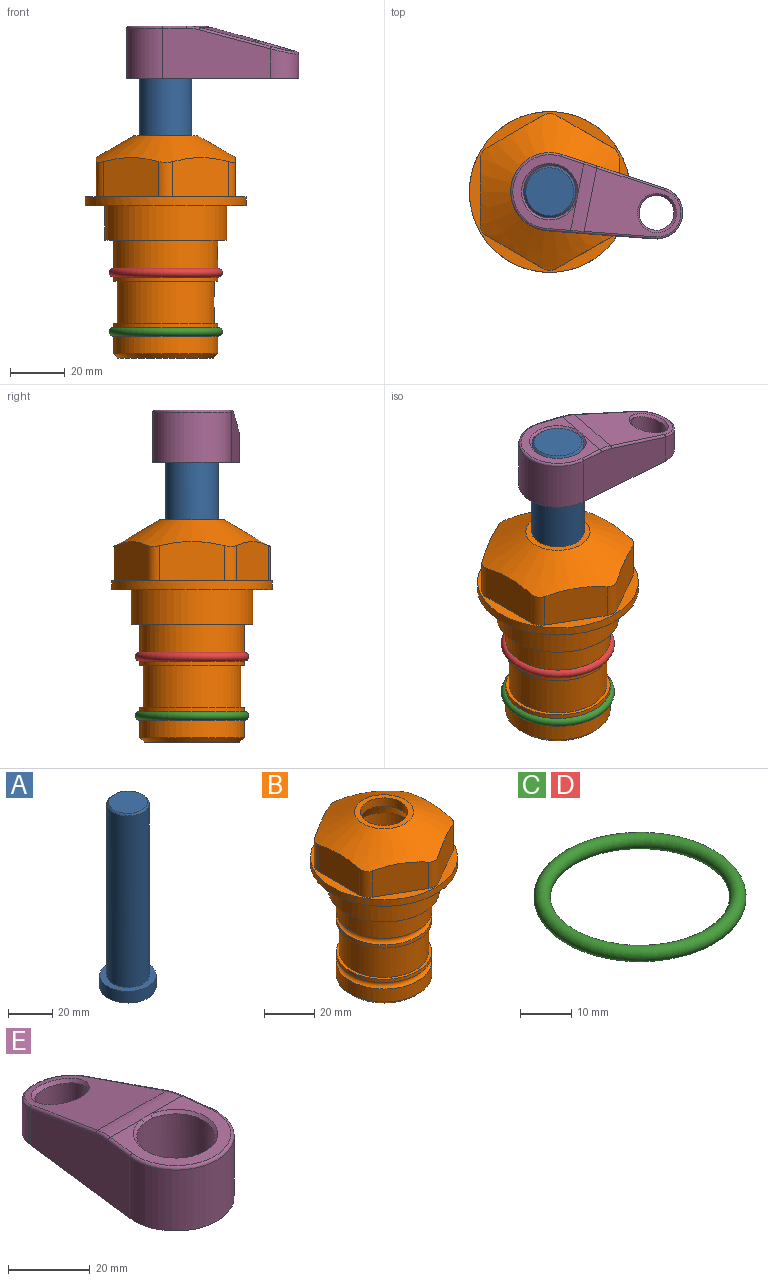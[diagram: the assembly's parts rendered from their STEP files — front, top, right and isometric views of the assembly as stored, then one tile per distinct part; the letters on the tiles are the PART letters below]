
ASSEMBLY  parts=5 mates=4
PART A: 6 faces, bbox 25.4x25.4x101.6 mm
  f0: plane 17.46x17.46mm, normal (0,0,1), area 239.5mm2, adj f5
  f1: plane 25.4x25.4mm, normal (0,0,-1), area 506.7mm2, adj f2
  f2: cylinder r=12.7mm len=25.4mm, axis (0,0,1), area 506.7mm2, adj f1,f3
  f3: plane 25.4x25.4mm, normal (0,0,1), area 221.7mm2, adj f2,f4
  f4: cylinder r=9.53mm len=94.46mm, axis (0,0,1), area 5653mm2, adj f3,f5
  f5: cone r=8.73mm half-angle=45deg, axis (0,0,-1), area 64.4mm2, adj f0,f4
PART B: 36 faces, bbox 58.7x58.7x81 mm
  f0: cylinder r=17.78mm len=35.56mm, axis (0,0,1), area 1670.8mm2, adj f23,f24,f31
  f1: cylinder r=19.05mm len=38.1mm, axis (0,0,1), area 1191.9mm2, adj f26,f27,f30
  f2: plane 58.66x58.66mm, normal (0,0,-1), area 1150.6mm2, adj f3,f28
  f3: cylinder r=29.33mm len=58.66mm, axis (0,0,-1), area 585.1mm2, adj f2,f4
  f4: plane 58.66x58.66mm, normal (0,0,1), area 475.9mm2, adj f3,f5,f6,f7,f8,f9,f10,f11
  f5: plane 20.32x14.34mm, normal (-0.5,0.87,0), area 324.4mm2, adj f4,f15,f16,f17
  f6: plane 20.32x14.34mm, normal (0.5,0.87,0), area 324.4mm2, adj f4,f14,f15,f17
  f7: plane 23.48x14.34mm, normal (1,0,0), area 324.4mm2, adj f4,f13,f14,f17
  f8: plane 20.32x14.34mm, normal (0.5,-0.87,0), area 324.4mm2, adj f4,f12,f13,f17
  f9: plane 20.32x14.34mm, normal (-0.5,-0.87,0), area 324.4mm2, adj f4,f11,f12,f17
  f10: plane 23.48x14.34mm, normal (-1,0,0), area 324.4mm2, adj f4,f11,f16,f17
  f11: cylinder r=5.08mm len=12.85mm, axis (0,0,-1), area 67.2mm2, adj f4,f9,f10,f17
  f12: cylinder r=5.08mm len=12.85mm, axis (0,0,-1), area 67.2mm2, adj f4,f8,f9,f17
  f13: cylinder r=5.08mm len=12.85mm, axis (0,0,-1), area 67.2mm2, adj f4,f7,f8,f17
  f14: cylinder r=5.08mm len=12.85mm, axis (0,0,-1), area 67.2mm2, adj f4,f6,f7,f17
  f15: cylinder r=5.08mm len=12.85mm, axis (0,0,-1), area 67.2mm2, adj f4,f5,f6,f17
  f16: cylinder r=5.08mm len=12.85mm, axis (0,0,-1), area 67.2mm2, adj f4,f5,f10,f17
  f17: cone r=11.73mm half-angle=60deg, axis (0,0,-1), area 2071.8mm2, adj f5,f6,f7,f8,f9,f10,f11,f12
  f18: plane 23.46x23.46mm, normal (0,0,1), area 147.4mm2, adj f17,f35
  f19: plane 34.93x34.93mm, normal (0,0,-1), area 958mm2, adj f29
  f20: cylinder r=19.05mm len=38.1mm, axis (0,0,1), area 760.1mm2, adj f21,f29
  f21: torus R=19.05mm, axis (0,0,1), area 565.3mm2, adj f20,f22
  f22: cylinder r=19.05mm len=38.1mm, axis (0,0,1), area 190mm2, adj f21,f23
  f23: plane 38.1x38.1mm, normal (0,0,1), area 146.9mm2, adj f0,f22
  f24: plane 38.1x38.1mm, normal (0,0,-1), area 146.9mm2, adj f0,f25
  f25: cylinder r=19.05mm len=38.1mm, axis (0,0,1), area 190mm2, adj f24,f26
  f26: torus R=19.05mm, axis (0,0,1), area 565.3mm2, adj f1,f25
  f27: plane 44.45x44.45mm, normal (0,0,-1), area 411.7mm2, adj f1,f28
  f28: cylinder r=22.23mm len=44.45mm, axis (0,0,1), area 1773.5mm2, adj f2,f27
  f29: cone r=19.05mm half-angle=45deg, axis (0,0,1), area 257.5mm2, adj f19,f20
  f30: cylinder r=3.17mm len=6.75mm, axis (-1,0,0), area 128mm2, adj f1,f33
  f31: cylinder r=3.17mm len=6.35mm, axis (-1,0,0), area 102.5mm2, adj f0,f33
  f32: plane 25.4x25.4mm, normal (0,0,1), area 506.7mm2, adj f33
  f33: cylinder r=12.7mm len=66.42mm, axis (0,0,-1), area 5236.2mm2, adj f30,f31,f32,f34
  f34: cone r=9.53mm half-angle=30deg, axis (0,0,-1), area 443.4mm2, adj f33,f35
  f35: cylinder r=9.53mm len=19.05mm, axis (0,0,-1), area 240.9mm2, adj f18,f34
PART C: 1 faces, bbox 44.7x44.7x3.2 mm
  f0: torus R=19.05mm, axis (0,0,1), area 1193.9mm2
PART D: same geometry as C
PART E: 31 faces, bbox 31.7x65.5x19.8 mm
  f0: plane 39.12x18.26mm, normal (0.99,0.12,0), area 612.2mm2, adj f1,f4,f7,f11,f13,f15
  f1: cylinder r=9.53mm len=18.91mm, axis (0,0,-1), area 296.1mm2, adj f0,f2,f7,f17
  f2: plane 39.12x18.26mm, normal (-0.99,0.12,0), area 612.2mm2, adj f1,f4,f7,f12,f14,f16
  f3: cylinder r=6.35mm len=12.7mm, axis (0,0,-1), area 362.4mm2, adj f7,f18
  f4: cylinder r=14.29mm len=28.58mm, axis (0,0,-1), area 882.2mm2, adj f0,f2,f7,f10
  f5: cylinder r=9.53mm len=19.05mm, axis (0,0,-1), area 1092.6mm2, adj f7,f19,f20
  f6: plane 26.99x23.69mm, normal (0,0,1), area 216.2mm2, adj f9,f10,f11,f12,f19
  f7: plane 63.5x28.58mm, normal (0,0,-1), area 661.8mm2, adj f0,f1,f2,f3,f4,f5,f22,f23
  f8: plane 33.52x23.6mm, normal (0,0.26,0.97), area 486mm2, adj f9,f15,f16,f17,f18
  f9: cylinder r=19.05mm len=24.72mm, axis (1,0,0), area 120.4mm2, adj f6,f8,f13,f14,f20
  f10: torus R=13.49mm, axis (0,0,1), area 59mm2, adj f4,f6,f11,f12
  f11: cylinder r=0.79mm len=8.67mm, axis (0.12,-0.99,0), area 10.8mm2, adj f0,f6,f10,f13
  f12: cylinder r=0.79mm len=8.67mm, axis (0.12,0.99,0), area 10.8mm2, adj f2,f6,f10,f14
  f13: bspline ~4.95x1.42mm, area 6.1mm2, adj f0,f9,f11,f15
  f14: bspline ~4.95x1.42mm, area 6.1mm2, adj f2,f9,f12,f16
  f15: cylinder r=0.79mm len=25.95mm, axis (0.12,-0.96,0.26), area 32.9mm2, adj f0,f8,f13,f17
  f16: cylinder r=0.79mm len=25.95mm, axis (0.12,0.96,-0.26), area 32.9mm2, adj f2,f8,f14,f17
  f17: bspline ~18.91x8.38mm, area 30mm2, adj f1,f8,f15,f16
  f18: bspline ~14.29x14.29mm, area 48.3mm2, adj f3,f8
  f19: cone r=9.53mm half-angle=45deg, axis (0,0,1), area 66.5mm2, adj f5,f6,f20
  f20: bspline ~3.22x0.96mm, area 3.5mm2, adj f5,f9,f19
  f21: plane 2.75x2.72mm, normal (0,0,-1), area 2.9mm2, adj f23,f25,f28
  f22: plane 23.05x15.88mm, normal (-0.99,-0.12,0), area 323.6mm2, adj f7,f25,f26,f27,f28,f29
  f23: plane 23.05x15.88mm, normal (0.99,-0.12,0), area 323.6mm2, adj f7,f21,f25,f27,f28,f30
  f24: cylinder r=9.53mm len=10.69mm, axis (0,0,-1), area 114.7mm2, adj f7,f27,f29,f30
  f25: cylinder r=12.7mm len=20.59mm, axis (0,0,-1), area 381.1mm2, adj f7,f21,f22,f23,f26,f28
  f26: plane 2.75x2.72mm, normal (0,0,-1), area 2.9mm2, adj f22,f25,f28
  f27: plane 19.72x18.37mm, normal (0,-0.26,-0.97), area 291.8mm2, adj f22,f23,f24,f28,f29,f30
  f28: cylinder r=15.88mm len=19.92mm, axis (1,0,0), area 54.8mm2, adj f21,f22,f23,f25,f26,f27
  f29: cylinder r=1.59mm len=11mm, axis (0,0,-1), area 34.7mm2, adj f7,f22,f24,f27
  f30: cylinder r=1.59mm len=11mm, axis (0,0,-1), area 34.7mm2, adj f7,f23,f24,f27
PLACE A rot(axis=(0,0,-1),101.2deg) t=(0,0,1.99)mm
PLACE B at identity fixed
PLACE C t=(0,0,-21.59)mm
PLACE D at identity
PLACE E rot(axis=(0,0,-1),101.2deg) t=(0,0,1.99)mm
MATE fastened C.f0 <-> B.f0  axis (0,0,1) through (0,0,-46.1)mm
MATE fastened E.f4 <-> A.f2  axis (0,0,1) through (0,0,65.49)mm
MATE fastened D.f0 <-> B.f0  axis (0,0,1) through (0,0,-24.51)mm
MATE cylindrical B.f0 <-> A.f2  axis (0,0,-1) through (0,0,21.37)mm
